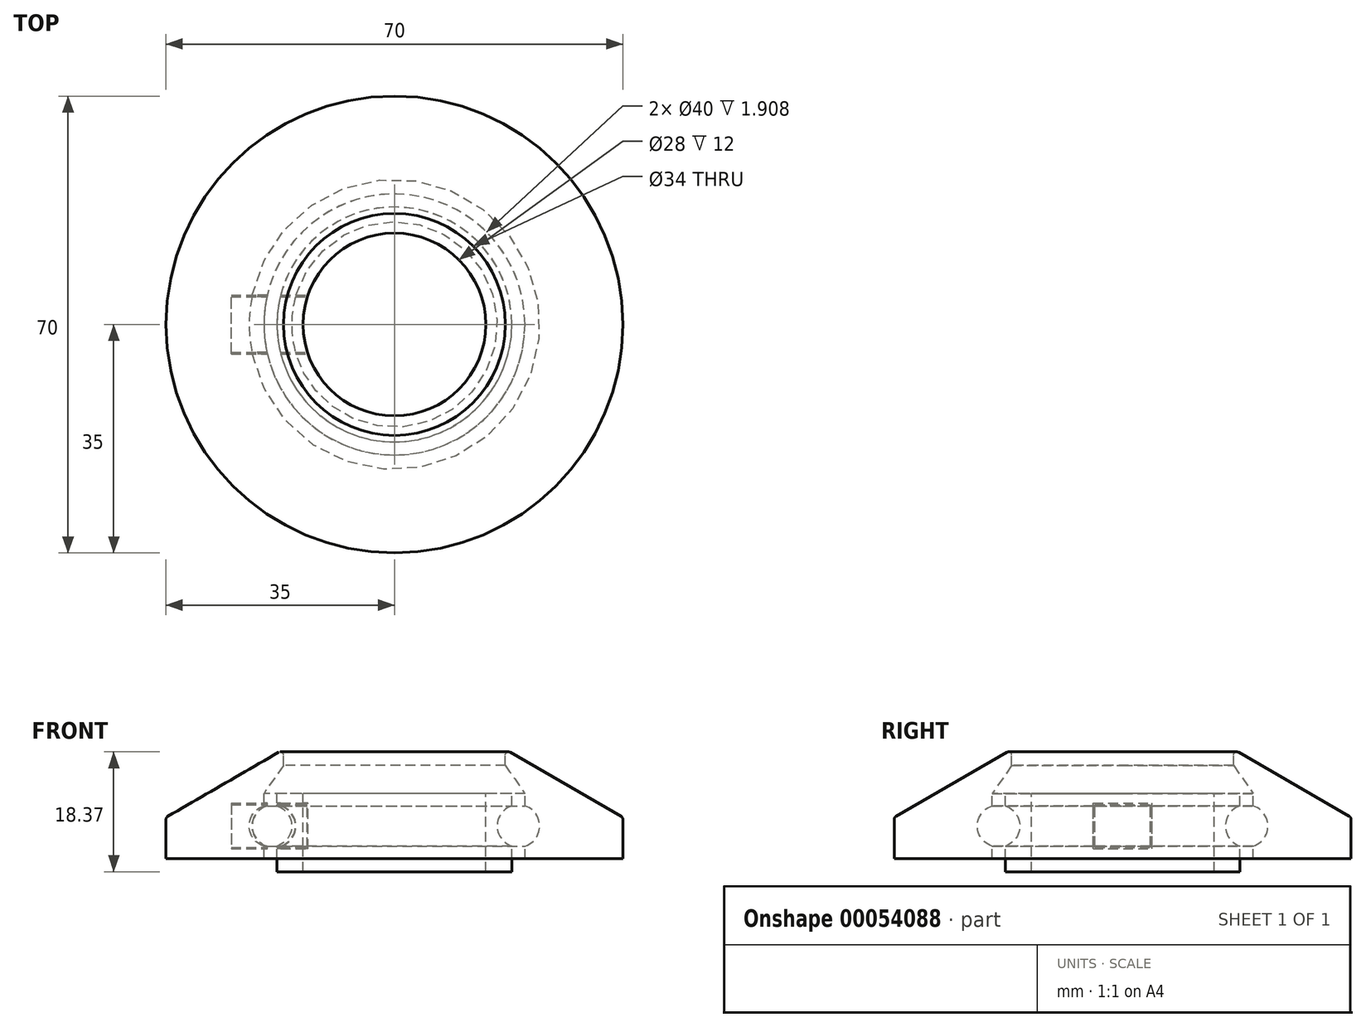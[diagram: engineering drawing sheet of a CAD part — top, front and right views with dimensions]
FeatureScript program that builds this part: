
annotation { "Feature Type Name" : "Feature", "Feature Type Description" : "" }
export const myFeature = defineFeature(function(context is Context, id is Id, definition is map)
    precondition{}
    {
        {
            var Q0;
            Q0=qCreatedBy(makeId("Right.planeOp"),FACE);
            var sketch = newSketch(context, id + "F0", { "sketchPlane" : qUnion([Q0])});
            skLineSegment(sketch, "E0.bottom", {"start": v(0, 0) * mm, "end": v(-4, 0) * mm});
            skLineSegment(sketch, "E0.top", {"start": v(0, 10) * mm, "end": v(-4, 10) * mm});
            skLineSegment(sketch, "E0.left", {"start": v(0, 0) * mm, "end": v(0, 1.9) * mm});
            skLineSegment(sketch, "E0.right", {"start": v(-4, 0) * mm, "end": v(-4, 10) * mm});
            skLineSegment(sketch, "E1.bottom", {"start": v(2, 0) * mm, "end": v(6, 0) * mm});
            skLineSegment(sketch, "E1.top", {"start": v(2, 10) * mm, "end": v(6, 10) * mm});
            skLineSegment(sketch, "E1.left", {"start": v(2, 0) * mm, "end": v(2, 1.9) * mm});
            skLineSegment(sketch, "E1.right", {"start": v(6, 0) * mm, "end": v(6, 10) * mm});
            skArc(sketch, "E2", {"start": v(0, 8.1) * mm, "mid": v(-2.25, 5) * mm, "end": v(0, 1.9) * mm});
            skLineSegment(sketch, "E3", {"start": v(-18, 26.88) * mm, "end": v(-18, -9.8) * mm, "construction": true});
            skLineSegment(sketch, "E4", {"start": v(2, 10) * mm, "end": v(2, 15) * mm});
            skLineSegment(sketch, "E5", {"start": v(-1, 16.73) * mm, "end": v(17, 6.34) * mm});
            skArc(sketch, "E6.trimOffspring", {"start": v(2, 1.9) * mm, "mid": v(4.25, 5) * mm, "end": v(2, 8.1) * mm});
            skLineSegment(sketch, "E7.trimOffspring", {"start": v(0, 8.1) * mm, "end": v(0, 10) * mm});
            skLineSegment(sketch, "E8.trimOffspring", {"start": v(2, 8.1) * mm, "end": v(2, 10) * mm});
            skLineSegment(sketch, "E9", {"start": v(17, 6.34) * mm, "end": v(17, 0) * mm});
            skLineSegment(sketch, "E10", {"start": v(17, 0) * mm, "end": v(6, 0) * mm});
            skLineSegment(sketch, "E11", {"start": v(-1, 16.73) * mm, "end": v(-1, 14.28) * mm});
            skLineSegment(sketch, "E12", {"start": v(-1, 14.28) * mm, "end": v(2, 10) * mm});
            skSolve(sketch);
        }
        {
            var Q0;
            Q0 = qSketchRegion(id + "F0", true);
            var Q1;
            Q1=sQuery(id+"F0.wireOp",EDGE,"E3");
            revolve(context, id + "F1", {"entities" : qUnion([Q0]), "axis" : qUnion([Q1]), "revolveType" : RevolveType.FULL});
        }
        {
            var Q0;
            Q0=qCreatedBy(makeId("Right.planeOp"),FACE);
            var sketch = newSketch(context, id + "F2", { "sketchPlane" : qUnion([Q0])});
            skLineSegment(sketch, "E13.0", {"start": v(-36, 10) * mm, "end": v(0, 10) * mm});
            skLineSegment(sketch, "E13.1", {"start": v(-36, 0) * mm, "end": v(0, 0) * mm});
            skLineSegment(sketch, "E14.bottom", {"start": v(-22.5, 8.5) * mm, "end": v(-13.5, 8.5) * mm});
            skLineSegment(sketch, "E14.top", {"start": v(-22.5, 1.5) * mm, "end": v(-13.5, 1.5) * mm});
            skLineSegment(sketch, "E14.left", {"start": v(-22.5, 8.5) * mm, "end": v(-22.5, 1.5) * mm});
            skLineSegment(sketch, "E14.right", {"start": v(-13.5, 8.5) * mm, "end": v(-13.5, 1.5) * mm});
            skLineSegment(sketch, "E15", {"start": v(-18, 14.93) * mm, "end": v(-18, 10) * mm, "construction": true});
            skLineSegment(sketch, "E16.0", {"start": v(-22.25, 8.25) * mm, "end": v(-13.75, 8.25) * mm});
            skLineSegment(sketch, "E16.1", {"start": v(-22.25, 8.25) * mm, "end": v(-22.25, 1.75) * mm});
            skLineSegment(sketch, "E16.2", {"start": v(-22.25, 1.75) * mm, "end": v(-13.75, 1.75) * mm});
            skLineSegment(sketch, "E16.3", {"start": v(-13.75, 8.25) * mm, "end": v(-13.75, 1.75) * mm});
            skSolve(sketch);
        }
        {
            var Q0;
            Q0 = qSketchRegion(id + "F2", true);
            extrude(context, id + "F3", {"entities" : qUnion([Q0]), "operationType" : NewBodyOperationType.REMOVE, "oppositeDirection" : true, "depth" : 25 * mm});
        }
        {
            var Q0;
            Q0=makeQuery(id+"F1.opRevolve","SWEPT_FACE",FACE,{"disambiguationData":[OSD([sQuery(id+"F0.wireOp",EDGE,"E0.bottom")])]});
            var sketch = newSketch(context, id + "F4", { "sketchPlane" : qUnion([Q0])});
            skSolve(sketch);
        }
        {
            var Q0;
            {var subQ0=sQuery(id+"F0.wireOp",EDGE,"E0.bottom");Q0=makeQuery(id+"F4.imprint","IMPRINT",FACE,{"disambiguationData":[TD([[makeQuery(id+"F4.imprint","IMPRINT",EDGE,{"derivedFrom":makeQuery(id+"F1.opRevolve","SWEPT_EDGE",EDGE,{"disambiguationData":[OSD([subQ0,sQuery(id+"F0.wireOp",EDGE,"E0.left")])]})}),-1.0]])]});}
            extrude(context, id + "F5", {"entities" : qUnion([Q0]), "operationType" : NewBodyOperationType.ADD, "depth" : 2 * mm});
        }
        {
            var Q0;
            Q0=makeQuery(id+"F1.opRevolve","SWEPT_EDGE",EDGE,{"disambiguationData":[OSD([sQuery(id+"F0.wireOp",EDGE,"E4"),sQuery(id+"F0.wireOp",EDGE,"E5")])]});
            fillet(context, id + "F6", {"entities" : qUnion([Q0]), "radius" : 0.5 * mm, "tangentPropagation" : true, "allowEdgeOverflow" : false});
        }
    });
